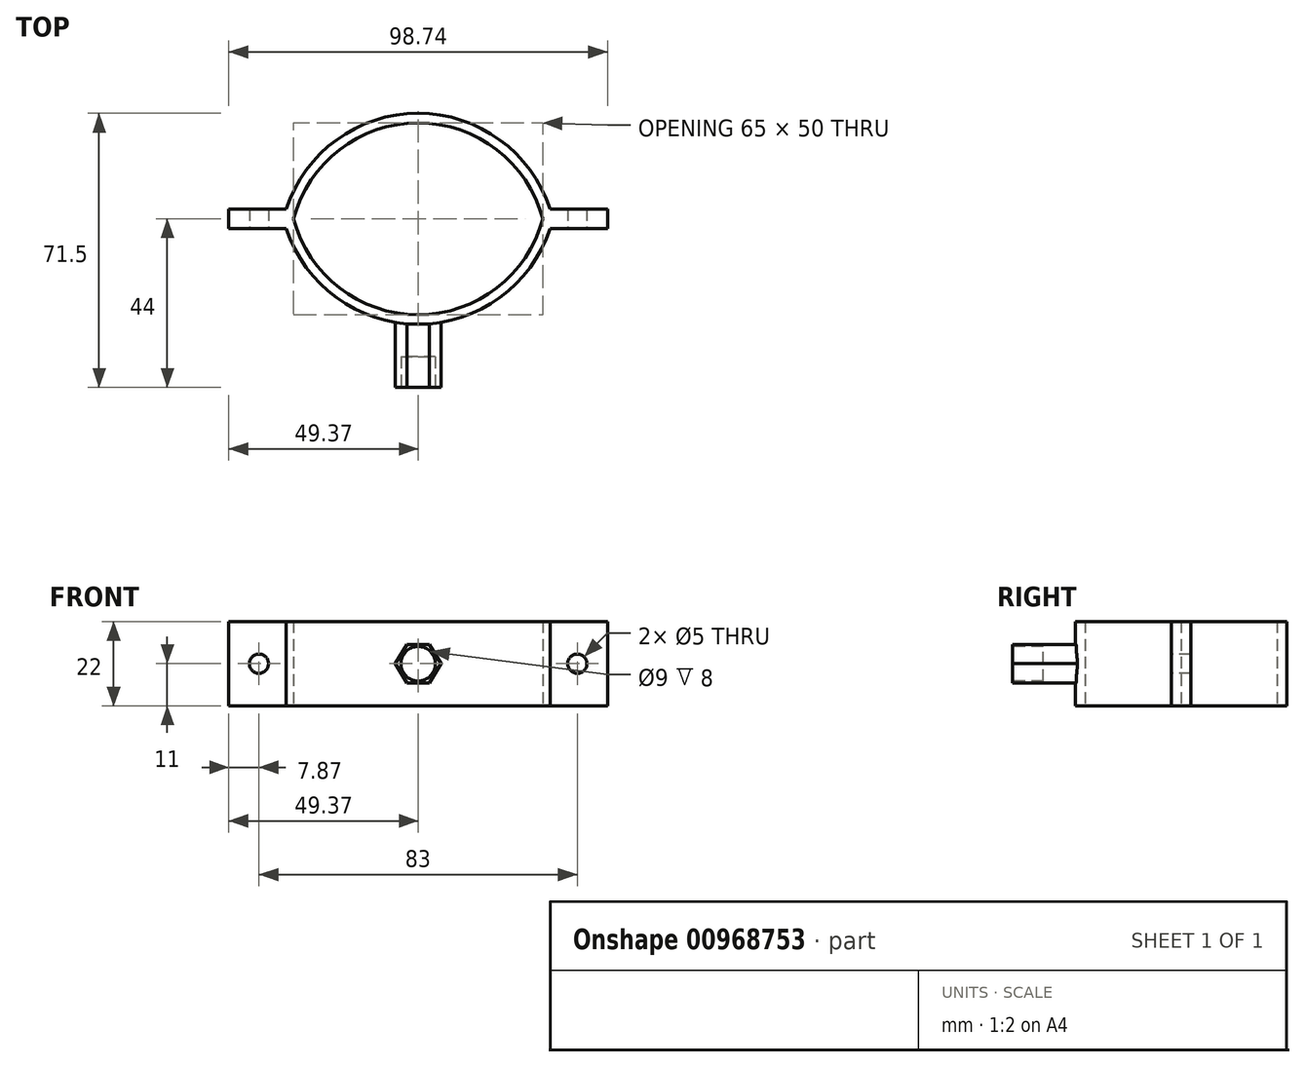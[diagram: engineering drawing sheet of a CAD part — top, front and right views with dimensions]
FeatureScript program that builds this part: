
annotation { "Feature Type Name" : "Feature", "Feature Type Description" : "" }
export const myFeature = defineFeature(function(context is Context, id is Id, definition is map)
    precondition{}
    {
        {
            var Q0;
            Q0=qCreatedBy(makeId("Top.planeOp"),FACE);
            var sketch = newSketch(context, id + "F0", { "sketchPlane" : qUnion([Q0])});
            skArc(sketch, "E0", {"start": v(32.5, 0) * mm, "mid": v(0, 25) * mm, "end": v(-32.5, 0) * mm});
            skLineSegment(sketch, "E1", {"start": v(-32.5, 0) * mm, "end": v(-49.37, 0) * mm});
            skLineSegment(sketch, "E2", {"start": v(-49.37, 0) * mm, "end": v(-49.37, 2.5) * mm});
            skLineSegment(sketch, "E3", {"start": v(-49.37, 2.5) * mm, "end": v(-34.37, 2.5) * mm});
            skLineSegment(sketch, "E4", {"start": v(32.5, 0) * mm, "end": v(49.37, 0) * mm});
            skLineSegment(sketch, "E5", {"start": v(49.37, 0) * mm, "end": v(49.37, 2.5) * mm});
            skLineSegment(sketch, "E6", {"start": v(49.37, 2.5) * mm, "end": v(34.37, 2.5) * mm});
            skArc(sketch, "E7", {"start": v(34.37, 2.5) * mm, "mid": v(0, 27.5) * mm, "end": v(-34.37, 2.5) * mm});
            skLineSegment(sketch, "E8.MirrorCS", {"start": v(49.37, 0) * mm, "end": v(49.37, -2.5) * mm});
            skLineSegment(sketch, "E9.MirrorCS", {"start": v(-49.37, 0) * mm, "end": v(-49.37, -2.5) * mm});
            skLineSegment(sketch, "E10.MirrorCS", {"start": v(-49.37, -2.5) * mm, "end": v(-34.37, -2.5) * mm});
            skLineSegment(sketch, "E11.MirrorCS", {"start": v(49.37, -2.5) * mm, "end": v(34.37, -2.5) * mm});
            skArc(sketch, "E12.MirrorCS", {"start": v(34.37, -2.5) * mm, "mid": v(0, -27.5) * mm, "end": v(-34.37, -2.5) * mm});
            skArc(sketch, "E13.MirrorCS", {"start": v(32.5, 0) * mm, "mid": v(0, -25) * mm, "end": v(-32.5, 0) * mm});
            skSolve(sketch);
        }
        {
            var Q0;
            Q0 = qSketchRegion(id + "F0", true);
            extrude(context, id + "F1", {"entities" : qUnion([Q0]), "depth" : 22 * mm, "offsetDistance" : 25 * mm});
        }
        {
            var Q0;
            Q0=qCreatedBy(makeId("Front.planeOp"),FACE);
            cPlane(context, id + "F2", {"entities" : qUnion([Q0]), "cplaneType" : CPlaneType.OFFSET, "offset" : 25 * mm, "width" : 150 * mm, "height" : 150 * mm});
        }
        {
            var Q0;
            Q0=qCreatedBy(id+"F2.planeOp",FACE);
            var sketch = newSketch(context, id + "F3", { "sketchPlane" : qUnion([Q0])});
            skLineSegment(sketch, "E14", {"start": v(2.93, 16) * mm, "end": v(-2.93, 16) * mm});
            skLineSegment(sketch, "E15", {"start": v(-2.93, 16) * mm, "end": v(-6, 11) * mm});
            skLineSegment(sketch, "E16", {"start": v(-6, 11) * mm, "end": v(-2.93, 6) * mm});
            skLineSegment(sketch, "E17", {"start": v(-2.93, 6) * mm, "end": v(2.93, 6) * mm});
            skLineSegment(sketch, "E18", {"start": v(2.93, 6) * mm, "end": v(6, 11) * mm});
            skLineSegment(sketch, "E19", {"start": v(2.93, 16) * mm, "end": v(6, 11) * mm});
            skSolve(sketch);
        }
        {
            var Q0;
            Q0 = qSketchRegion(id + "F3", true);
            extrude(context, id + "F4", {"entities" : qUnion([Q0]), "operationType" : NewBodyOperationType.ADD, "depth" : 19 * mm, "offsetDistance" : 25 * mm});
        }
        {
            var Q0;
            Q0=makeQuery(id+"F1.opExtrude","SWEPT_FACE",FACE,{"disambiguationData":[OSD([sQuery(id+"F0.wireOp",EDGE,"E11.MirrorCS")])]});
            var sketch = newSketch(context, id + "F5", { "sketchPlane" : qUnion([Q0])});
            skCircle(sketch, "E20", {"center": v(41.5, 11) * mm, "radius": 2.5 * mm});
            skCircle(sketch, "E21", {"center": v(-41.5, 11) * mm, "radius": 2.5 * mm});
            skSolve(sketch);
        }
        {
            var Q0;
            Q0 = qSketchRegion(id + "F5", true);
            extrude(context, id + "F6", {"entities" : qUnion([Q0]), "operationType" : NewBodyOperationType.REMOVE, "endBound" : BoundingType.UP_TO_NEXT, "oppositeDirection" : true, "depth" : 25 * mm, "offsetDistance" : 25 * mm});
        }
        {
            var Q0;
            Q0=makeQuery(id+"F4.opExtrude","CAP_FACE",FACE,{"disambiguationData":[OSD([sQuery(id+"F3.wireOp",EDGE,"E14"),sQuery(id+"F3.wireOp",EDGE,"E15"),sQuery(id+"F3.wireOp",EDGE,"E16"),sQuery(id+"F3.wireOp",EDGE,"E17"),sQuery(id+"F3.wireOp",EDGE,"E18"),sQuery(id+"F3.wireOp",EDGE,"E19")])],"isStart":false});
            var sketch = newSketch(context, id + "F7", { "sketchPlane" : qUnion([Q0])});
            skCircle(sketch, "E22", {"center": v(0, 11) * mm, "radius": 4.5 * mm});
            skSolve(sketch);
        }
        {
            var Q0;
            Q0 = qSketchRegion(id + "F7", true);
            extrude(context, id + "F8", {"entities" : qUnion([Q0]), "operationType" : NewBodyOperationType.REMOVE, "oppositeDirection" : true, "depth" : 8 * mm, "offsetDistance" : 25 * mm});
        }
    });
